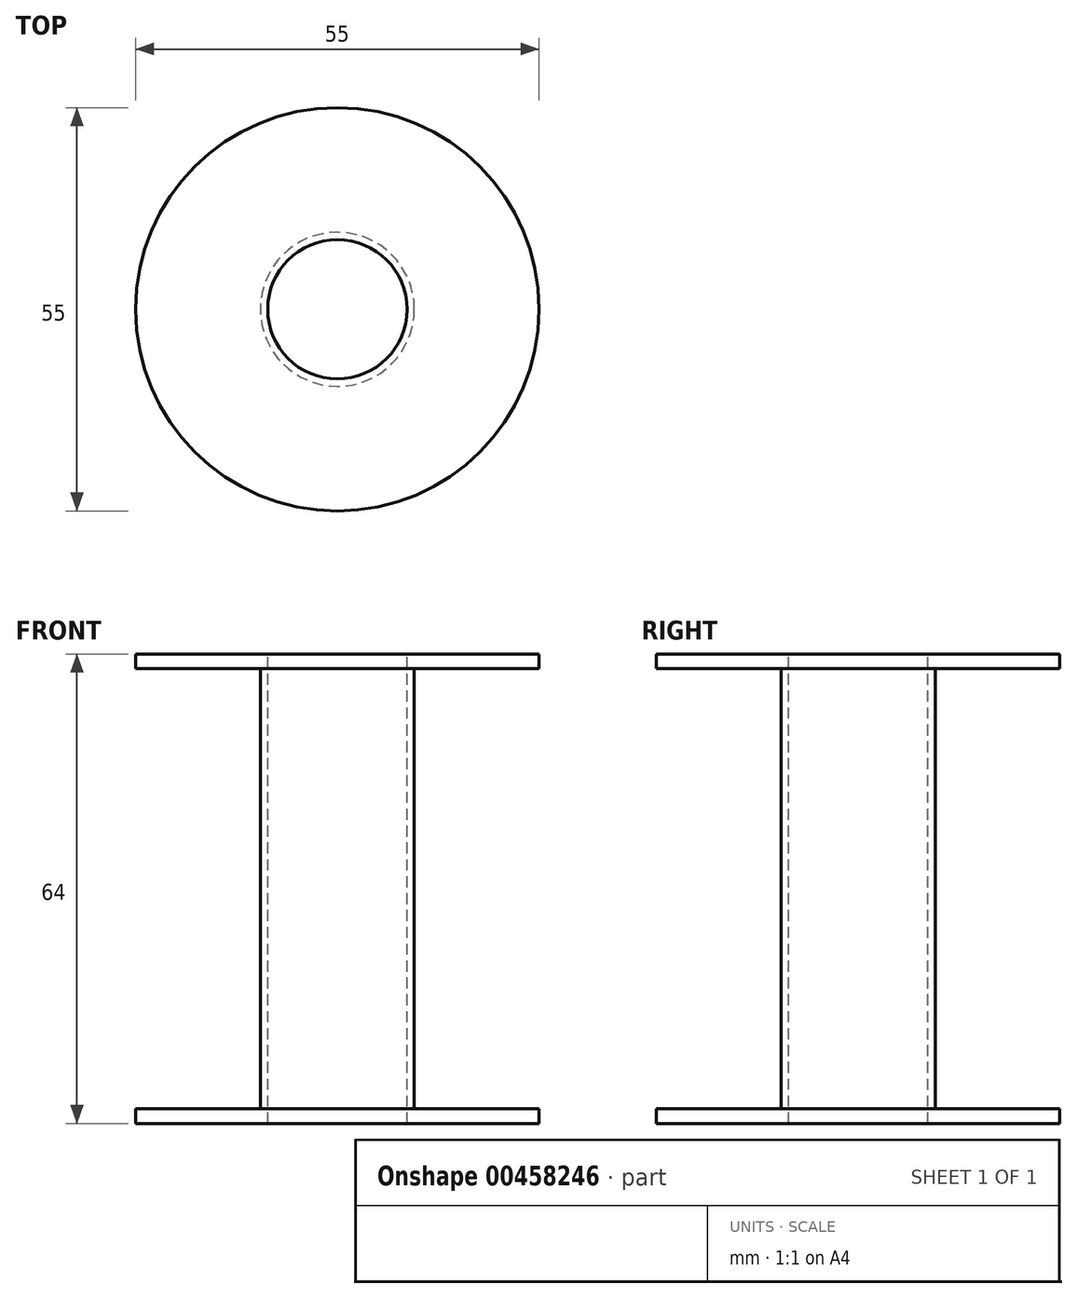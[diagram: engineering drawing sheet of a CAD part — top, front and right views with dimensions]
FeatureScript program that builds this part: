
annotation { "Feature Type Name" : "Feature", "Feature Type Description" : "" }
export const myFeature = defineFeature(function(context is Context, id is Id, definition is map)
    precondition{}
    {
        {
            var Q0;
            Q0=qCreatedBy(makeId("Top.planeOp"),FACE);
            var sketch = newSketch(context, id + "F0", { "sketchPlane" : qUnion([Q0])});
            skCircle(sketch, "E0", {"center": v(0, 0) * mm, "radius": 27.5 * mm});
            skSolve(sketch);
        }
        {
            var Q0;
            Q0=qCreatedBy(makeId("Top.planeOp"),FACE);
            var sketch = newSketch(context, id + "F1", { "sketchPlane" : qUnion([Q0])});
            skCircle(sketch, "E1", {"center": v(0, 0) * mm, "radius": 10.5 * mm});
            skSolve(sketch);
        }
        {
            var Q0;
            Q0 = qSketchRegion(id + "F0", true);
            extrude(context, id + "F2", {"entities" : qUnion([Q0]), "depth" : 2 * mm});
        }
        {
            var Q0;
            Q0 = qSketchRegion(id + "F1", true);
            extrude(context, id + "F3", {"entities" : qUnion([Q0]), "operationType" : NewBodyOperationType.ADD, "oppositeDirection" : true, "depth" : 60 * mm});
        }
        {
            var Q0;
            Q0=makeQuery(id+"F3.opExtrude","CAP_FACE",FACE,{"disambiguationData":[OSD([sQuery(id+"F1.wireOp",EDGE,"E1")])],"isStart":false});
            var sketch = newSketch(context, id + "F4", { "sketchPlane" : qUnion([Q0])});
            skCircle(sketch, "E2", {"center": v(0, 0) * mm, "radius": 27.5 * mm});
            skSolve(sketch);
        }
        {
            var Q0;
            Q0 = qSketchRegion(id + "F4", true);
            extrude(context, id + "F5", {"entities" : qUnion([Q0]), "operationType" : NewBodyOperationType.ADD, "depth" : 2 * mm});
        }
        {
            var Q0;
            Q0=makeQuery(id+"F2.opExtrude","CAP_FACE",FACE,{"disambiguationData":[OSD([sQuery(id+"F0.wireOp",EDGE,"E0")])],"isStart":false});
            var sketch = newSketch(context, id + "F6", { "sketchPlane" : qUnion([Q0])});
            skCircle(sketch, "E3", {"center": v(0, 0) * mm, "radius": 9.5 * mm});
            skSolve(sketch);
        }
        {
            var Q0;
            Q0 = qSketchRegion(id + "F6", true);
            var Q1;
            Q1=makeQuery(id+"F5.opExtrude","CAP_FACE",FACE,{"disambiguationData":[OSD([sQuery(id+"F4.wireOp",EDGE,"E2")])],"isStart":false});
            extrude(context, id + "F7", {"entities" : qUnion([Q0]), "operationType" : NewBodyOperationType.REMOVE, "endBound" : BoundingType.UP_TO_SURFACE, "oppositeDirection" : true, "endBoundEntityFace" : qUnion([Q1]), "depth" : 25 * mm});
        }
    });
